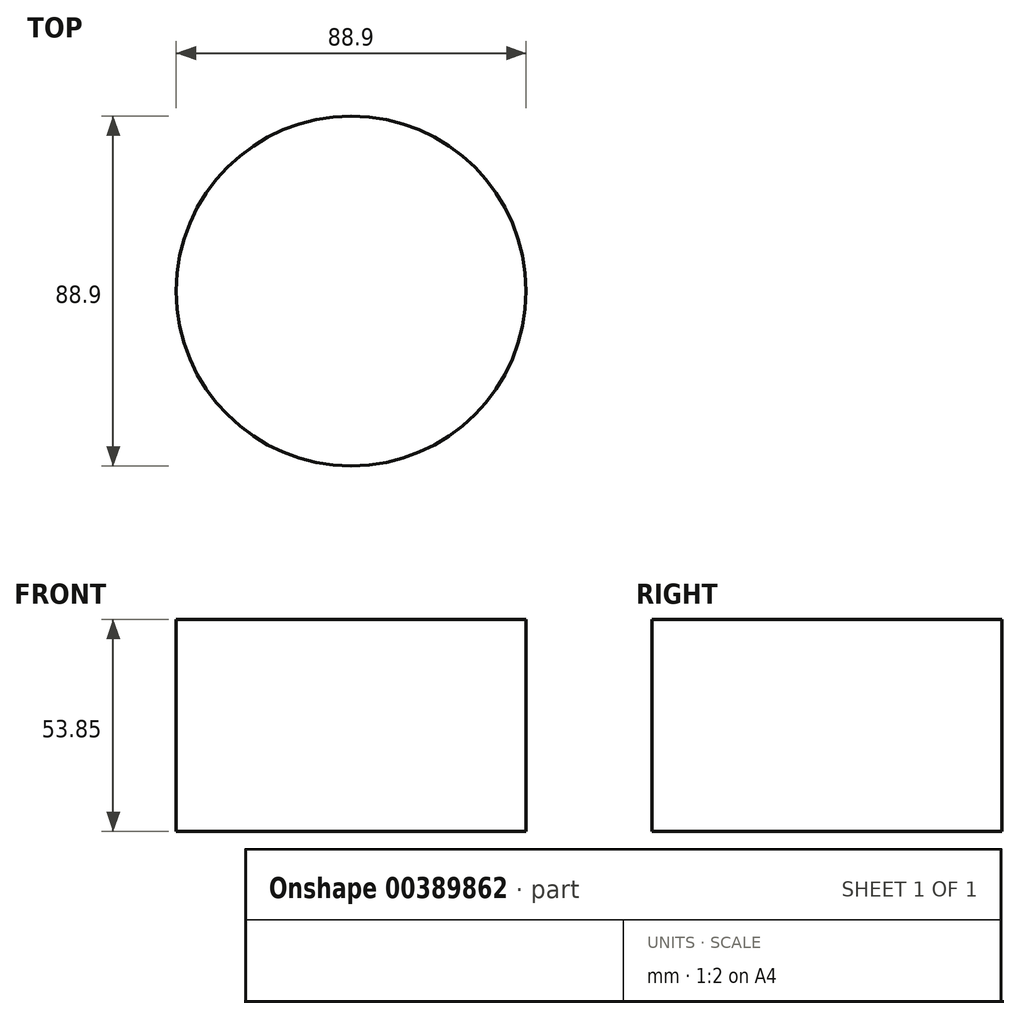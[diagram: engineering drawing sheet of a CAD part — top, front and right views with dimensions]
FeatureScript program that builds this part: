
annotation { "Feature Type Name" : "Feature", "Feature Type Description" : "" }
export const myFeature = defineFeature(function(context is Context, id is Id, definition is map)
    precondition{}
    {
        {
            var Q0;
            Q0=qCreatedBy(makeId("Top.planeOp"),FACE);
            var sketch = newSketch(context, id + "F0", { "sketchPlane" : qUnion([Q0])});
            skCircle(sketch, "E0", {"center": v(0, 0) * mm, "radius": 44.45 * mm});
            skSolve(sketch);
        }
        {
            var Q0;
            Q0 = qSketchRegion(id + "F0", true);
            extrude(context, id + "F1", {"entities" : qUnion([Q0]), "depth" : 53.85 * mm});
        }
    });
